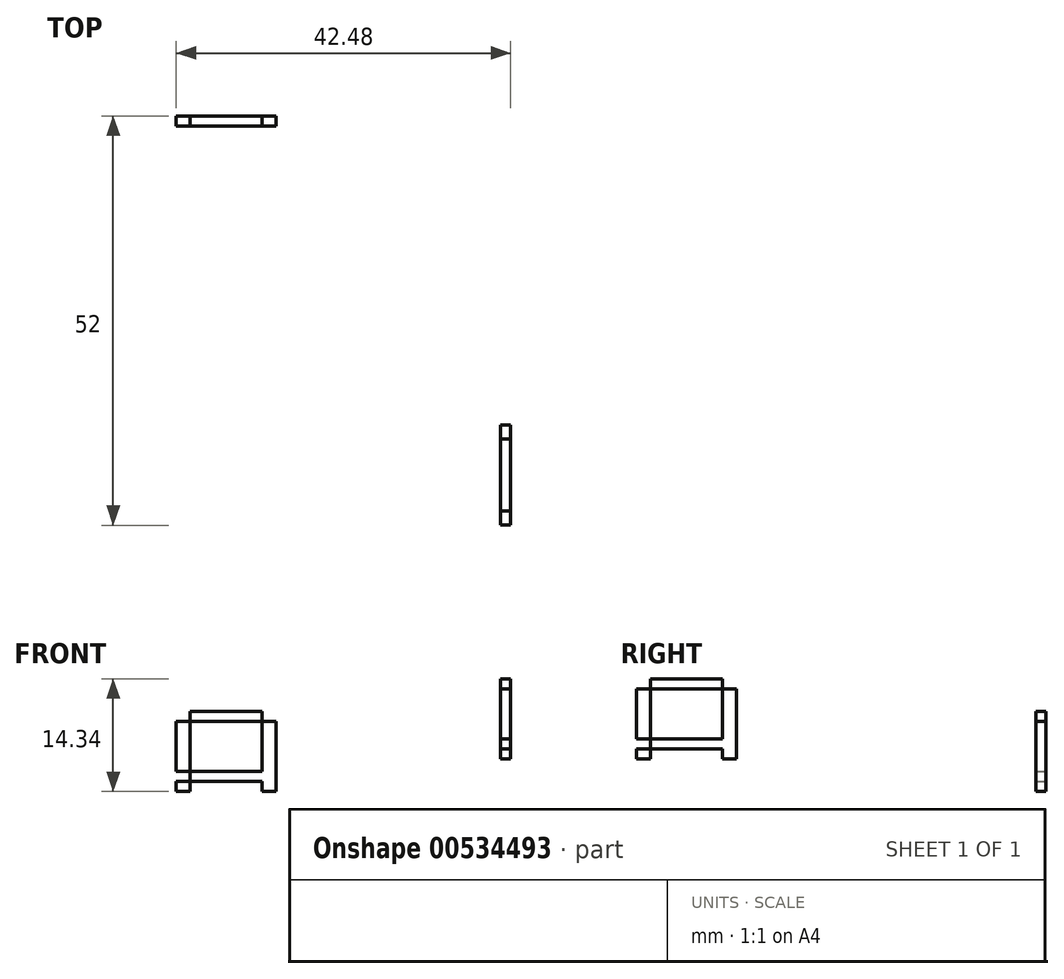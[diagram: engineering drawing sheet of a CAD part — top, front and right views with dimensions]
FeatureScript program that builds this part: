
annotation { "Feature Type Name" : "Feature", "Feature Type Description" : "" }
export const myFeature = defineFeature(function(context is Context, id is Id, definition is map)
    precondition{}
    {
        {
            var Q0;
            Q0=qCreatedBy(makeId("Front.planeOp"),FACE);
            var sketch = newSketch(context, id + "F0", { "sketchPlane" : qUnion([Q0])});
            skLineSegment(sketch, "E0.bottom", {"start": v(-41.84, 19.83) * mm, "end": v(-40.06, 19.83) * mm});
            skLineSegment(sketch, "E0.top", {"start": v(-41.84, 9.67) * mm, "end": v(-40.06, 9.67) * mm});
            skLineSegment(sketch, "E0.left", {"start": v(-41.84, 19.83) * mm, "end": v(-41.84, 9.67) * mm});
            skLineSegment(sketch, "E0.right", {"start": v(-40.06, 19.83) * mm, "end": v(-40.06, 9.67) * mm});
            skLineSegment(sketch, "E1.bottom", {"start": v(-41.84, 10.94) * mm, "end": v(-29.14, 10.94) * mm});
            skLineSegment(sketch, "E1.top", {"start": v(-41.84, 12.2) * mm, "end": v(-29.14, 12.2) * mm});
            skLineSegment(sketch, "E1.left", {"start": v(-41.84, 10.94) * mm, "end": v(-41.84, 12.2) * mm});
            skLineSegment(sketch, "E1.right", {"start": v(-29.14, 10.94) * mm, "end": v(-29.14, 12.2) * mm});
            skLineSegment(sketch, "E2.bottom", {"start": v(-41.84, 19.83) * mm, "end": v(-29.14, 19.83) * mm});
            skLineSegment(sketch, "E2.top", {"start": v(-41.84, 18.56) * mm, "end": v(-29.14, 18.56) * mm});
            skLineSegment(sketch, "E2.left", {"start": v(-41.84, 19.83) * mm, "end": v(-41.84, 18.56) * mm});
            skLineSegment(sketch, "E2.right", {"start": v(-29.14, 19.83) * mm, "end": v(-29.14, 18.56) * mm});
            skLineSegment(sketch, "E3.bottom", {"start": v(-29.14, 19.83) * mm, "end": v(-30.92, 19.83) * mm});
            skLineSegment(sketch, "E3.top", {"start": v(-29.14, 9.67) * mm, "end": v(-30.92, 9.67) * mm});
            skLineSegment(sketch, "E3.left", {"start": v(-29.14, 19.83) * mm, "end": v(-29.14, 9.67) * mm});
            skLineSegment(sketch, "E3.right", {"start": v(-30.92, 19.83) * mm, "end": v(-30.92, 9.67) * mm});
            skSolve(sketch);
        }
        {
            var Q0;
            {var subQ0=sQuery(id+"F0.wireOp",EDGE,"E1.bottom");var subQ1=sQuery(id+"F0.wireOp",EDGE,"E0.right");var subQ2=makeQuery(id+"F0.imprint","INTERSECT",VERTEX,{"derivedFrom":[subQ1,subQ0]});Q0=makeQuery(id+"F0.imprint","IMPRINT",FACE,{"disambiguationData":[TD([[makeQuery(id+"F0.imprint","IMPRINT",EDGE,{"disambiguationData":[TD([[subQ2,1.0]])],"derivedFrom":subQ1}),1.0]])]});}
            var Q1;
            {var subQ0=sQuery(id+"F0.wireOp",EDGE,"E3.left");var subQ1=sQuery(id+"F0.wireOp",EDGE,"E1.bottom");var subQ2=makeQuery(id+"F0.imprint","INTERSECT",VERTEX,{"derivedFrom":[subQ1,subQ0]});Q1=makeQuery(id+"F0.imprint","IMPRINT",FACE,{"disambiguationData":[TD([[makeQuery(id+"F0.imprint","IMPRINT",EDGE,{"disambiguationData":[TD([[subQ2,1.0]])],"derivedFrom":subQ1}),1.0]])]});}
            var Q2;
            {var subQ5=sQuery(id+"F0.wireOp",EDGE,"E3.top");Q2=makeQuery(id+"F0.imprint","IMPRINT",FACE,{"disambiguationData":[TD([[makeQuery(id+"F0.imprint","IMPRINT",EDGE,{"derivedFrom":subQ5}),-1.0]])]});}
            var Q3;
            {var subQ0=sQuery(id+"F0.wireOp",EDGE,"E0.top");Q3=makeQuery(id+"F0.imprint","IMPRINT",FACE,{"disambiguationData":[TD([[makeQuery(id+"F0.imprint","IMPRINT",EDGE,{"derivedFrom":subQ0}),1.0]])]});}
            var Q4;
            {var subQ5=sQuery(id+"F0.wireOp",EDGE,"E1.left");Q4=makeQuery(id+"F0.imprint","IMPRINT",FACE,{"disambiguationData":[TD([[makeQuery(id+"F0.imprint","IMPRINT",EDGE,{"derivedFrom":subQ5}),-1.0]])]});}
            var Q5;
            {var subQ0=sQuery(id+"F0.wireOp",EDGE,"E2.top");var subQ5=sQuery(id+"F0.wireOp",EDGE,"E0.right");var subQ6=makeQuery(id+"F0.imprint","INTERSECT",VERTEX,{"derivedFrom":[subQ5,subQ0]});Q5=makeQuery(id+"F0.imprint","IMPRINT",FACE,{"disambiguationData":[TD([[makeQuery(id+"F0.imprint","IMPRINT",EDGE,{"disambiguationData":[TD([[subQ6,-1.0]])],"derivedFrom":subQ5}),-1.0]])]});}
            var Q6;
            {var subQ5=sQuery(id+"F0.wireOp",EDGE,"E2.left");Q6=makeQuery(id+"F0.imprint","IMPRINT",FACE,{"disambiguationData":[TD([[makeQuery(id+"F0.imprint","IMPRINT",EDGE,{"derivedFrom":subQ5}),1.0]])]});}
            var Q7;
            {var subQ0=sQuery(id+"F0.wireOp",EDGE,"E2.bottom");var subQ1=sQuery(id+"F0.wireOp",EDGE,"E0.right");var subQ2=makeQuery(id+"F0.imprint","INTERSECT",VERTEX,{"derivedFrom":[subQ1,subQ0]});Q7=makeQuery(id+"F0.imprint","IMPRINT",FACE,{"disambiguationData":[TD([[makeQuery(id+"F0.imprint","IMPRINT",EDGE,{"disambiguationData":[TD([[subQ2,-1.0]])],"derivedFrom":subQ1}),1.0]])]});}
            var Q8;
            {var subQ0=sQuery(id+"F0.wireOp",EDGE,"E3.left");var subQ1=sQuery(id+"F0.wireOp",EDGE,"E1.top");var subQ2=makeQuery(id+"F0.imprint","INTERSECT",VERTEX,{"derivedFrom":[subQ1,subQ0]});Q8=makeQuery(id+"F0.imprint","IMPRINT",FACE,{"disambiguationData":[TD([[makeQuery(id+"F0.imprint","IMPRINT",EDGE,{"disambiguationData":[TD([[subQ2,1.0]])],"derivedFrom":subQ1}),1.0]])]});}
            var Q9;
            {var subQ5=sQuery(id+"F0.wireOp",EDGE,"E3.bottom");Q9=makeQuery(id+"F0.imprint","IMPRINT",FACE,{"disambiguationData":[TD([[makeQuery(id+"F0.imprint","IMPRINT",EDGE,{"derivedFrom":subQ5}),1.0]])]});}
            extrude(context, id + "F1", {"entities" : qUnion([Q0, Q1, Q2, Q3, Q4, Q5, Q6, Q7, Q8, Q9]), "endBound" : BoundingType.SYMMETRIC, "depth" : 1.27 * mm, "offsetDistance" : 25.4 * mm});
        }
        {
            var Q0;
            Q0=qCreatedBy(makeId("Right.planeOp"),FACE);
            var sketch = newSketch(context, id + "F2", { "sketchPlane" : qUnion([Q0])});
            skLineSegment(sketch, "E4.bottom", {"start": v(-51.36, 24) * mm, "end": v(-49.58, 24) * mm});
            skLineSegment(sketch, "E4.top", {"start": v(-51.36, 13.85) * mm, "end": v(-49.58, 13.85) * mm});
            skLineSegment(sketch, "E4.left", {"start": v(-51.36, 24) * mm, "end": v(-51.36, 13.85) * mm});
            skLineSegment(sketch, "E4.right", {"start": v(-49.58, 24) * mm, "end": v(-49.58, 13.85) * mm});
            skLineSegment(sketch, "E5.bottom", {"start": v(-51.36, 15.12) * mm, "end": v(-38.66, 15.12) * mm});
            skLineSegment(sketch, "E5.top", {"start": v(-51.36, 16.39) * mm, "end": v(-38.66, 16.39) * mm});
            skLineSegment(sketch, "E5.left", {"start": v(-51.36, 15.12) * mm, "end": v(-51.36, 16.39) * mm});
            skLineSegment(sketch, "E5.right", {"start": v(-38.66, 15.12) * mm, "end": v(-38.66, 16.39) * mm});
            skLineSegment(sketch, "E6.bottom", {"start": v(-51.36, 24) * mm, "end": v(-38.66, 24) * mm});
            skLineSegment(sketch, "E6.top", {"start": v(-51.36, 22.74) * mm, "end": v(-38.66, 22.74) * mm});
            skLineSegment(sketch, "E6.left", {"start": v(-51.36, 24) * mm, "end": v(-51.36, 22.74) * mm});
            skLineSegment(sketch, "E6.right", {"start": v(-38.66, 24) * mm, "end": v(-38.66, 22.74) * mm});
            skLineSegment(sketch, "E7.bottom", {"start": v(-38.66, 24) * mm, "end": v(-40.43, 24) * mm});
            skLineSegment(sketch, "E7.top", {"start": v(-38.66, 13.85) * mm, "end": v(-40.43, 13.85) * mm});
            skLineSegment(sketch, "E7.left", {"start": v(-38.66, 24) * mm, "end": v(-38.66, 13.85) * mm});
            skLineSegment(sketch, "E7.right", {"start": v(-40.43, 24) * mm, "end": v(-40.43, 13.85) * mm});
            skSolve(sketch);
        }
        {
            var Q0;
            {var subQ0=sQuery(id+"F2.wireOp",EDGE,"E4.top");Q0=makeQuery(id+"F2.imprint","IMPRINT",FACE,{"disambiguationData":[TD([[makeQuery(id+"F2.imprint","IMPRINT",EDGE,{"derivedFrom":subQ0}),1.0]])]});}
            var Q1;
            {var subQ5=sQuery(id+"F2.wireOp",EDGE,"E5.left");Q1=makeQuery(id+"F2.imprint","IMPRINT",FACE,{"disambiguationData":[TD([[makeQuery(id+"F2.imprint","IMPRINT",EDGE,{"derivedFrom":subQ5}),-1.0]])]});}
            var Q2;
            {var subQ0=sQuery(id+"F2.wireOp",EDGE,"E6.top");var subQ5=sQuery(id+"F2.wireOp",EDGE,"E4.right");var subQ6=makeQuery(id+"F2.imprint","INTERSECT",VERTEX,{"derivedFrom":[subQ5,subQ0]});Q2=makeQuery(id+"F2.imprint","IMPRINT",FACE,{"disambiguationData":[TD([[makeQuery(id+"F2.imprint","IMPRINT",EDGE,{"disambiguationData":[TD([[subQ6,-1.0]])],"derivedFrom":subQ5}),-1.0]])]});}
            var Q3;
            {var subQ0=sQuery(id+"F2.wireOp",EDGE,"E7.left");var subQ1=sQuery(id+"F2.wireOp",EDGE,"E5.top");var subQ2=makeQuery(id+"F2.imprint","INTERSECT",VERTEX,{"derivedFrom":[subQ1,subQ0]});Q3=makeQuery(id+"F2.imprint","IMPRINT",FACE,{"disambiguationData":[TD([[makeQuery(id+"F2.imprint","IMPRINT",EDGE,{"disambiguationData":[TD([[subQ2,1.0]])],"derivedFrom":subQ1}),1.0]])]});}
            var Q4;
            {var subQ0=sQuery(id+"F2.wireOp",EDGE,"E7.left");var subQ1=sQuery(id+"F2.wireOp",EDGE,"E5.bottom");var subQ2=makeQuery(id+"F2.imprint","INTERSECT",VERTEX,{"derivedFrom":[subQ1,subQ0]});Q4=makeQuery(id+"F2.imprint","IMPRINT",FACE,{"disambiguationData":[TD([[makeQuery(id+"F2.imprint","IMPRINT",EDGE,{"disambiguationData":[TD([[subQ2,1.0]])],"derivedFrom":subQ1}),1.0]])]});}
            var Q5;
            {var subQ5=sQuery(id+"F2.wireOp",EDGE,"E7.top");Q5=makeQuery(id+"F2.imprint","IMPRINT",FACE,{"disambiguationData":[TD([[makeQuery(id+"F2.imprint","IMPRINT",EDGE,{"derivedFrom":subQ5}),-1.0]])]});}
            var Q6;
            {var subQ0=sQuery(id+"F2.wireOp",EDGE,"E5.bottom");var subQ1=sQuery(id+"F2.wireOp",EDGE,"E4.right");var subQ2=makeQuery(id+"F2.imprint","INTERSECT",VERTEX,{"derivedFrom":[subQ1,subQ0]});Q6=makeQuery(id+"F2.imprint","IMPRINT",FACE,{"disambiguationData":[TD([[makeQuery(id+"F2.imprint","IMPRINT",EDGE,{"disambiguationData":[TD([[subQ2,1.0]])],"derivedFrom":subQ1}),1.0]])]});}
            var Q7;
            {var subQ0=sQuery(id+"F2.wireOp",EDGE,"E6.bottom");var subQ1=sQuery(id+"F2.wireOp",EDGE,"E4.right");var subQ2=makeQuery(id+"F2.imprint","INTERSECT",VERTEX,{"derivedFrom":[subQ1,subQ0]});Q7=makeQuery(id+"F2.imprint","IMPRINT",FACE,{"disambiguationData":[TD([[makeQuery(id+"F2.imprint","IMPRINT",EDGE,{"disambiguationData":[TD([[subQ2,-1.0]])],"derivedFrom":subQ1}),1.0]])]});}
            var Q8;
            {var subQ5=sQuery(id+"F2.wireOp",EDGE,"E6.left");Q8=makeQuery(id+"F2.imprint","IMPRINT",FACE,{"disambiguationData":[TD([[makeQuery(id+"F2.imprint","IMPRINT",EDGE,{"derivedFrom":subQ5}),1.0]])]});}
            var Q9;
            {var subQ5=sQuery(id+"F2.wireOp",EDGE,"E7.bottom");Q9=makeQuery(id+"F2.imprint","IMPRINT",FACE,{"disambiguationData":[TD([[makeQuery(id+"F2.imprint","IMPRINT",EDGE,{"derivedFrom":subQ5}),1.0]])]});}
            extrude(context, id + "F3", {"entities" : qUnion([Q0, Q1, Q2, Q3, Q4, Q5, Q6, Q7, Q8, Q9]), "endBound" : BoundingType.SYMMETRIC, "depth" : 1.27 * mm, "offsetDistance" : 25.4 * mm});
        }
    });
